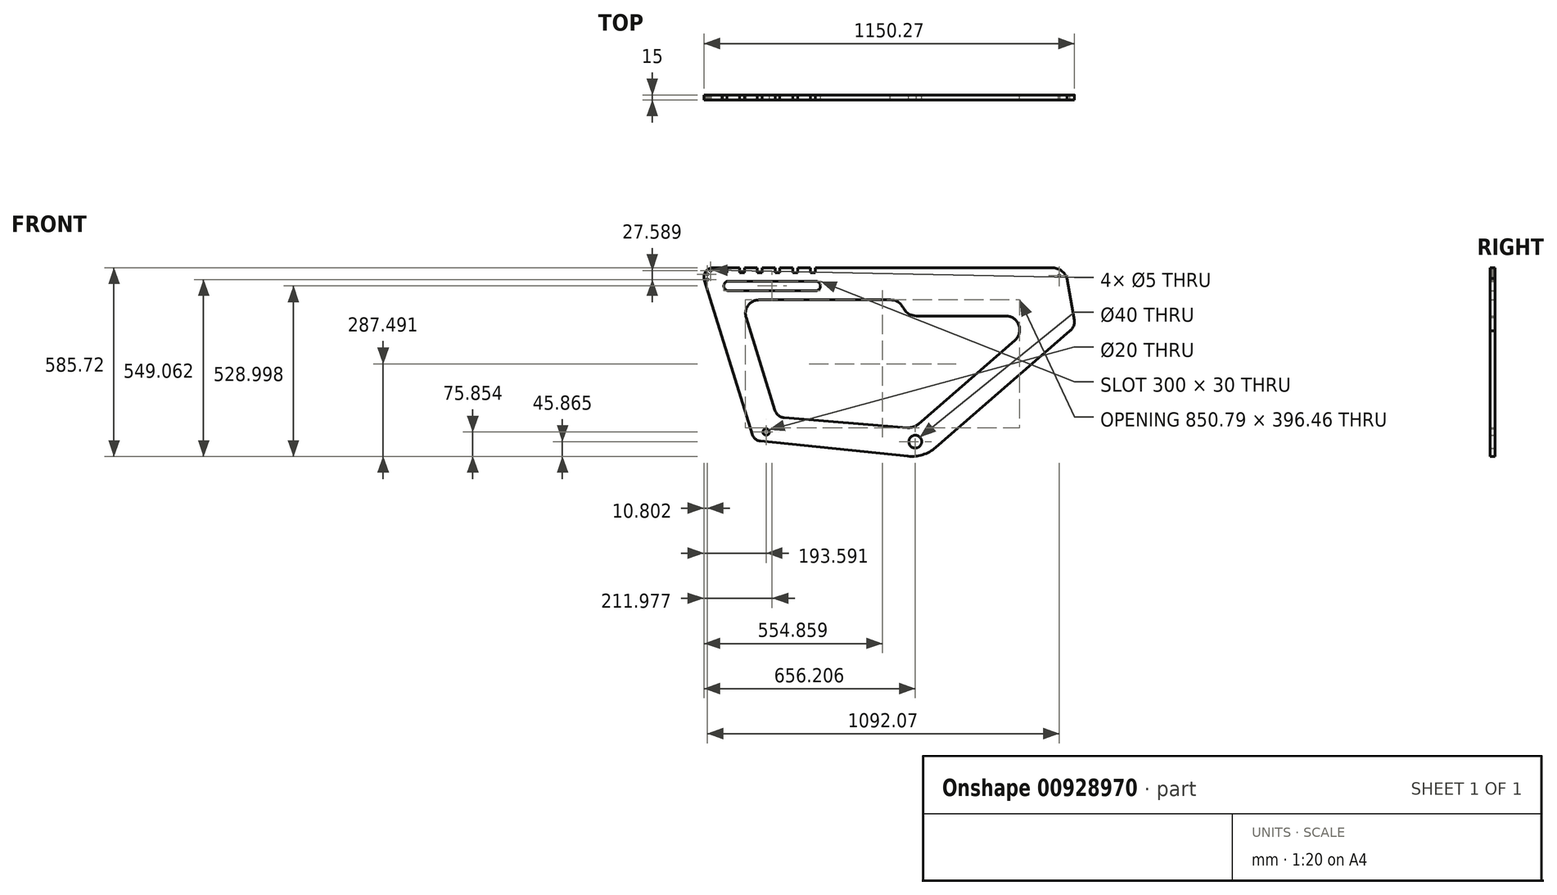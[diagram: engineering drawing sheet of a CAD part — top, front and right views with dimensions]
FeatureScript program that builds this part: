
annotation { "Feature Type Name" : "Feature", "Feature Type Description" : "" }
export const myFeature = defineFeature(function(context is Context, id is Id, definition is map)
    precondition{}
    {
        {
            var Q0;
            Q0=qCreatedBy(makeId("Front.planeOp"),FACE);
            var sketch = newSketch(context, id + "F0", { "sketchPlane" : qUnion([Q0])});
            skLineSegment(sketch, "E0", {"start": v(-250.26, -41.74) * mm, "end": v(207.32, -88.8) * mm});
            skLineSegment(sketch, "E1", {"start": v(-424.47, 456.8) * mm, "end": v(-276.02, -20.66) * mm});
            skLineSegment(sketch, "E2", {"start": v(293.4, -61.58) * mm, "end": v(709.6, 299.96) * mm});
            skArc(sketch, "E3", {"start": v(-276.02, -20.66) * mm, "mid": v(-266.3, -35.07) * mm, "end": v(-250.26, -41.74) * mm});
            skLineSegment(sketch, "E4", {"start": v(-294.76, 342.76) * mm, "end": v(-205.03, 54.15) * mm});
            skLineSegment(sketch, "E5", {"start": v(239.64, 10.94) * mm, "end": v(539.84, 271.71) * mm});
            skLineSegment(sketch, "E6", {"start": v(701.38, 462.39) * mm, "end": v(723.93, 333.53) * mm});
            skArc(sketch, "E7", {"start": v(207.32, -88.8) * mm, "mid": v(253.19, -84.12) * mm, "end": v(293.4, -61.58) * mm});
            skLineSegment(sketch, "E8", {"start": v(-254.58, 396.32) * mm, "end": v(152.18, 396.32) * mm});
            skLineSegment(sketch, "E9", {"start": v(511.96, 346.32) * mm, "end": v(234.05, 346.32) * mm});
            skFitSpline(sketch, "E10", {"points": [v(152.18, 396.32) * mm, v(234.05, 346.32) * mm], "startDerivative": vector(152.16, -1.58) * mm, "endDerivative": vector(156.1, -11.33) * mm});
            skLineSegment(sketch, "E11.bottom", {"start": v(-369.7, 496.32) * mm, "end": v(-354.7, 496.32) * mm});
            skLineSegment(sketch, "E11.top", {"start": v(-369.7, 481.32) * mm, "end": v(-354.7, 481.32) * mm});
            skLineSegment(sketch, "E11.left", {"start": v(-369.7, 496.32) * mm, "end": v(-369.7, 481.32) * mm});
            skLineSegment(sketch, "E11.right", {"start": v(-354.7, 496.32) * mm, "end": v(-354.7, 481.32) * mm});
            skLineSegment(sketch, "E12.bottom", {"start": v(-348.86, 454.6) * mm, "end": v(-78.86, 454.6) * mm});
            skLineSegment(sketch, "E12.top", {"start": v(-348.86, 424.6) * mm, "end": v(-78.86, 424.6) * mm});
            skArc(sketch, "E13", {"start": v(-78.86, 424.6) * mm, "mid": v(-63.86, 439.6) * mm, "end": v(-78.86, 454.6) * mm});
            skArc(sketch, "E14", {"start": v(-348.86, 454.6) * mm, "mid": v(-363.86, 439.6) * mm, "end": v(-348.86, 424.6) * mm});
            skLineSegment(sketch, "E15.bottom", {"start": v(-314.7, 496.32) * mm, "end": v(-299.7, 496.32) * mm});
            skLineSegment(sketch, "E15.top", {"start": v(-314.7, 481.32) * mm, "end": v(-299.7, 481.32) * mm});
            skLineSegment(sketch, "E15.left", {"start": v(-314.7, 496.32) * mm, "end": v(-314.7, 481.32) * mm});
            skLineSegment(sketch, "E15.right", {"start": v(-299.7, 496.32) * mm, "end": v(-299.7, 481.32) * mm});
            skLineSegment(sketch, "E16.bottom", {"start": v(-259.7, 496.32) * mm, "end": v(-244.7, 496.32) * mm});
            skLineSegment(sketch, "E16.top", {"start": v(-259.7, 481.32) * mm, "end": v(-244.7, 481.32) * mm});
            skLineSegment(sketch, "E16.left", {"start": v(-259.7, 496.32) * mm, "end": v(-259.7, 481.32) * mm});
            skLineSegment(sketch, "E16.right", {"start": v(-244.7, 496.32) * mm, "end": v(-244.7, 481.32) * mm});
            skLineSegment(sketch, "E17.bottom", {"start": v(-204.7, 496.32) * mm, "end": v(-189.7, 496.32) * mm});
            skLineSegment(sketch, "E17.top", {"start": v(-204.7, 481.32) * mm, "end": v(-189.7, 481.32) * mm});
            skLineSegment(sketch, "E17.left", {"start": v(-204.7, 496.32) * mm, "end": v(-204.7, 481.32) * mm});
            skLineSegment(sketch, "E17.right", {"start": v(-189.7, 496.32) * mm, "end": v(-189.7, 481.32) * mm});
            skLineSegment(sketch, "E18.bottom", {"start": v(-149.7, 496.32) * mm, "end": v(-134.7, 496.32) * mm});
            skLineSegment(sketch, "E18.top", {"start": v(-149.7, 481.32) * mm, "end": v(-134.7, 481.32) * mm});
            skLineSegment(sketch, "E18.left", {"start": v(-149.7, 496.32) * mm, "end": v(-149.7, 481.32) * mm});
            skLineSegment(sketch, "E18.right", {"start": v(-134.7, 496.32) * mm, "end": v(-134.7, 481.32) * mm});
            skLineSegment(sketch, "E19.bottom", {"start": v(-94.7, 496.32) * mm, "end": v(-79.7, 496.32) * mm});
            skLineSegment(sketch, "E19.top", {"start": v(-94.7, 481.32) * mm, "end": v(-79.7, 481.32) * mm});
            skLineSegment(sketch, "E19.left", {"start": v(-94.7, 496.32) * mm, "end": v(-94.7, 481.32) * mm});
            skLineSegment(sketch, "E19.right", {"start": v(-79.7, 496.32) * mm, "end": v(-79.7, 481.32) * mm});
            skCircle(sketch, "E20", {"center": v(-232.25, -13.55) * mm, "radius": 10 * mm});
            skCircle(sketch, "E21", {"center": v(230.37, -43.54) * mm, "radius": 20 * mm});
            skLineSegment(sketch, "E22", {"start": v(-395.36, 496.32) * mm, "end": v(654.64, 496.32) * mm});
            skArc(sketch, "E23", {"start": v(-395.36, 496.32) * mm, "mid": v(-419.9, 483.91) * mm, "end": v(-424.47, 456.8) * mm});
            skLineSegment(sketch, "E24", {"start": v(-552.23, 546.32) * mm, "end": v(-62.69, 546.32) * mm});
            skArc(sketch, "E25", {"start": v(701.38, 462.39) * mm, "mid": v(683.51, 486.94) * mm, "end": v(654.64, 496.32) * mm});
            skArc(sketch, "E26", {"start": v(709.6, 299.96) * mm, "mid": v(721.75, 314.62) * mm, "end": v(723.93, 333.53) * mm});
            skArc(sketch, "E27", {"start": v(-254.58, 396.32) * mm, "mid": v(-288.06, 379.58) * mm, "end": v(-294.76, 342.76) * mm});
            skArc(sketch, "E28", {"start": v(539.84, 271.71) * mm, "mid": v(551.79, 318.69) * mm, "end": v(511.96, 346.32) * mm});
            skLineSegment(sketch, "E29", {"start": v(-567.52, -105.42) * mm, "end": v(-102.94, -105.42) * mm});
            skLineSegment(sketch, "E30", {"start": v(-175.75, 30.72) * mm, "end": v(206.36, 0) * mm});
            skArc(sketch, "E31", {"start": v(-205.03, 54.15) * mm, "mid": v(-193.98, 37.95) * mm, "end": v(-175.75, 30.72) * mm});
            skLineSegment(sketch, "E32", {"start": v(222.93, 583.17) * mm, "end": v(825.25, 583.17) * mm});
            skArc(sketch, "E33", {"start": v(206.36, 0) * mm, "mid": v(224.1, 2.11) * mm, "end": v(239.64, 10.94) * mm});
            skCircle(sketch, "E34", {"center": v(-404.46, 487.25) * mm, "radius": 2.5 * mm});
            skCircle(sketch, "E35", {"center": v(-414.95, 476.15) * mm, "radius": 2.5 * mm});
            skCircle(sketch, "E36", {"center": v(-415.04, 459.66) * mm, "radius": 2.5 * mm});
            skCircle(sketch, "E37", {"center": v(677.03, 471.78) * mm, "radius": 2.5 * mm});
            skSolve(sketch);
        }
        {
            var Q0;
            Q0=makeQuery(id+"F0.imprint","IMPRINT",FACE,{"disambiguationData":[TD([[makeQuery(id+"F0.imprint","IMPRINT",EDGE,{"derivedFrom":sQuery(id+"F0.wireOp",EDGE,"E0")}),1.0]])]});
            extrude(context, id + "F1", {"entities" : qUnion([Q0]), "endBound" : BoundingType.SYMMETRIC, "depth" : 15 * mm, "offsetDistance" : 25 * mm});
        }
    });
